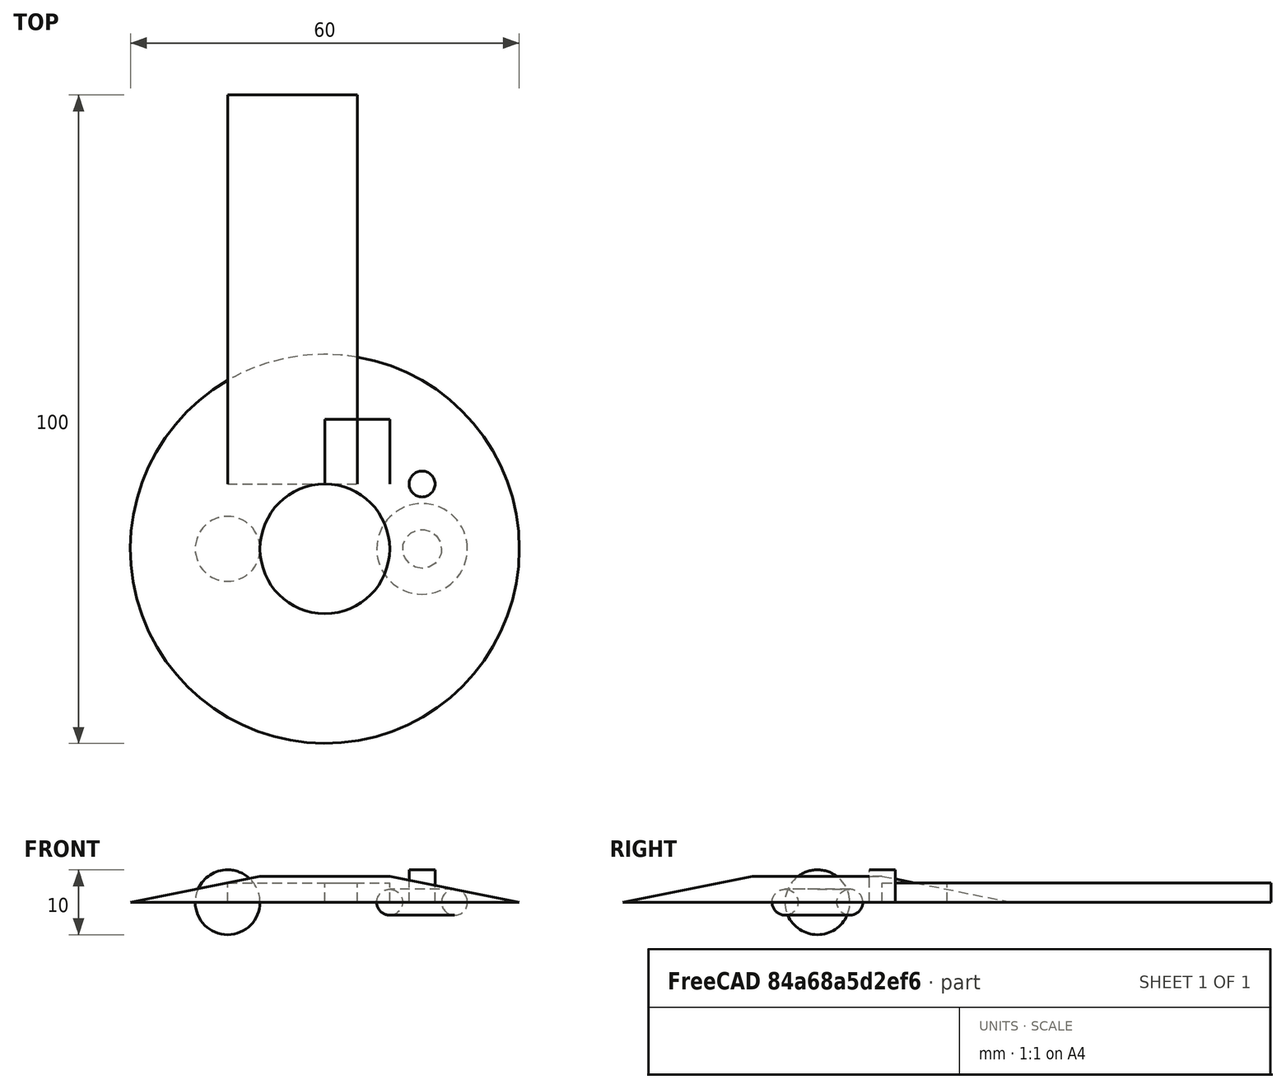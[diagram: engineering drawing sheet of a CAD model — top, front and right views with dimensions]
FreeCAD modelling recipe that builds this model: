
FCSTD DOCUMENT  (FreeCAD 0.16R6703 (Git))
Label: shapes-test2
License: All rights reserved
LicenseURL: http://en.wikipedia.org/wiki/All_rights_reserved
objects: Part::Box×2, Part::Cylinder×1, Part::Sphere×1, Part::Cone×1, Part::Torus×1
note: 6 computed .brp shape members not serialized (recipe doc carries the construction recipe); baked Part::Feature solids carry a one-line shape summary decoded from their .brp

FEATURE [Part::Box] Box  label="Cube"
  Height = 3
  Length = 10
  Placement = pos=(15,0,0) rot=(0,0,1;0rad)
  Width = 10
FEATURE [Part::Box] Box001  label="Cube001"
  Height = 3
  Length = 20
  Width = 60
FEATURE [Part::Cylinder] Cylinder
  Angle = 360
  Height = 5
  Placement = pos=(30,0,0) rot=(0,0,1;0rad)
  Radius = 2
FEATURE [Part::Sphere] Sphere
  Angle1 = -90
  Angle2 = 90
  Angle3 = 360
  Placement = pos=(0,-10,0) rot=(0,0,1;0rad)
  Radius = 5
FEATURE [Part::Cone] Cone
  Angle = 360
  Height = 4
  Placement = pos=(15,-10,0) rot=(0,0,1;0rad)
  Radius1 = 30
  Radius2 = 10
FEATURE [Part::Torus] Torus
  Angle1 = -180
  Angle2 = 180
  Angle3 = 360
  Placement = pos=(30,-10,0) rot=(0,0,1;0rad)
  Radius1 = 5
  Radius2 = 2
